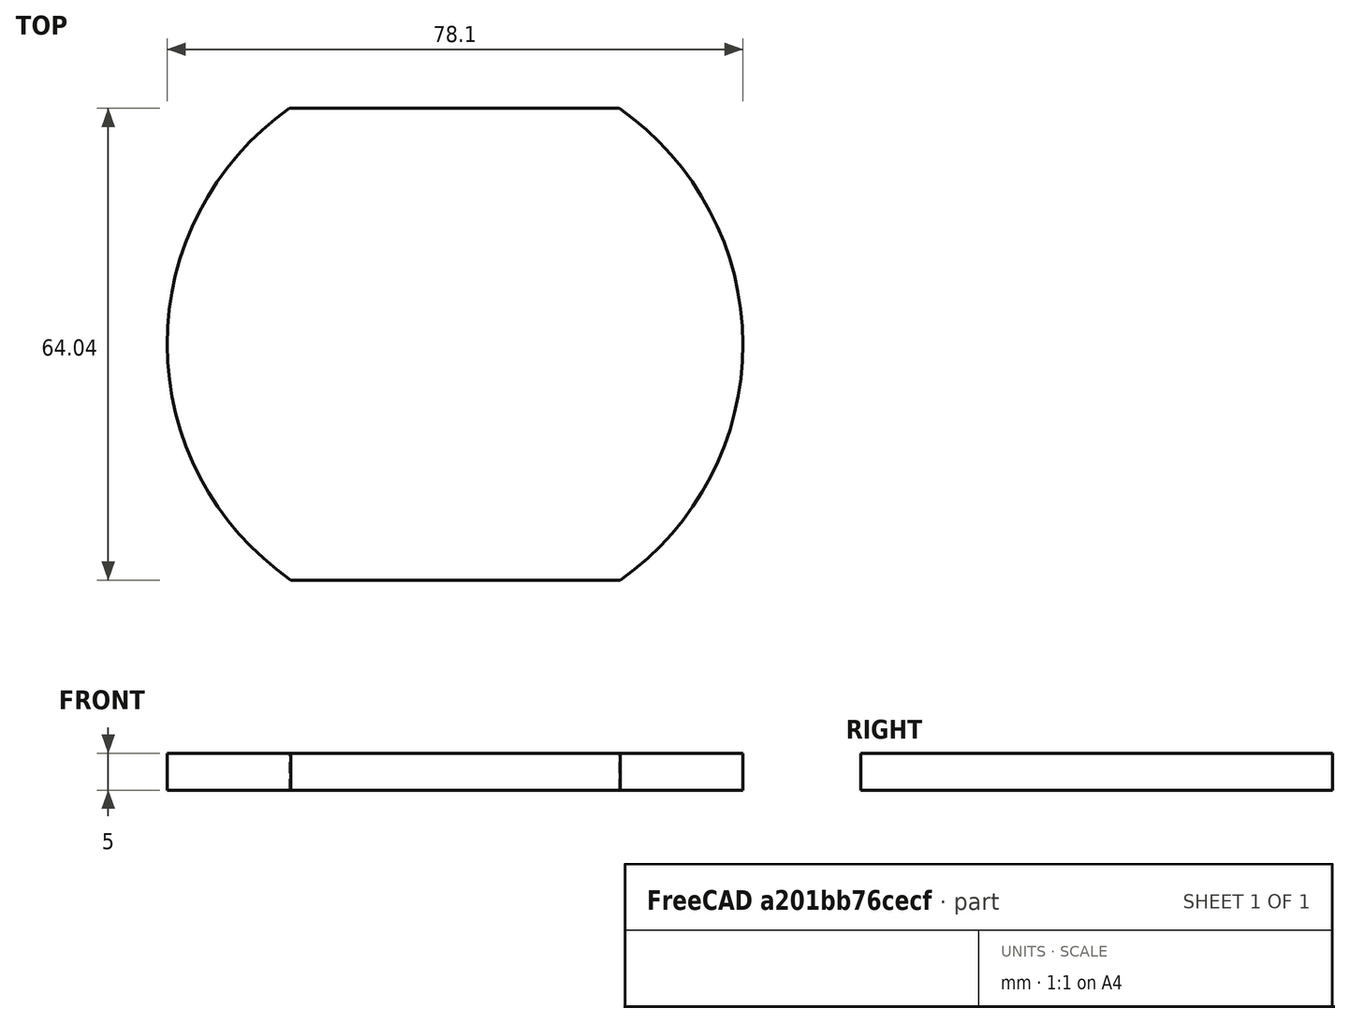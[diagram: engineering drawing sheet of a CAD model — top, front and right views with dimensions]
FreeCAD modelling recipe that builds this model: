
FCSTD DOCUMENT  (FreeCAD 1.0R39319 (Git))
Label: test_chord_volume
License: All rights reserved
LicenseURL: https://en.wikipedia.org/wiki/All_rights_reserved
objects: Sketcher::SketchObject×1, PartDesign::Pad×1, PartDesign::Body×1
note: 6 computed .brp shape members not serialized (recipe doc carries the construction recipe); baked Part::Feature solids carry a one-line shape summary decoded from their .brp

FEATURE [Sketcher::SketchObject] Sketch_1
  ArcFitTolerance = 1e-06
  AttachmentSupport = -> [XY_Plane]
  FullyConstrained = false
  MakeInternals = false
  MapMode = 5
  sketch-geometry (4):
    g0: ArcOfCircle CenterX=-0.00134482 CenterY=-7.04804 CenterZ=0 NormalX=0 NormalY=0 NormalZ=1 AngleXU=0 Radius=39.0492 StartAngle=5.32437 EndAngle=7.24728
    g1: LineSegment StartX=22.2629 StartY=25.0323 StartZ=0 EndX=-22.4507 EndY=25.0323 EndZ=0
    g2: ArcOfCircle CenterX=0.00211821 CenterY=-6.92347 CenterZ=0 NormalX=0 NormalY=0 NormalZ=1 AngleXU=0 Radius=39.0551 StartAngle=2.18328 EndAngle=4.10577
    g3: LineSegment StartX=-22.2629 StartY=-39.0104 StartZ=0 EndX=22.4319 EndY=-39.0104 EndZ=0
  constraints (7):
    c: Coincident(g0,g1)
    c: Coincident(g1,g2)
    c: Coincident(g2,g3)
    c: Coincident(g3,g0)
    c: Parallel(g1,g3)
    c: Horizontal(g1)
    c: Distance(g1,g3) = 78
FEATURE [PartDesign::Pad] Pad_1
  Direction = (0,0,1)
  Length = 5
  Length2 = 10
  Profile = -> Sketch_1
  Refine = true
  Suppressed = false
  Type = 0
FEATURE [PartDesign::Body] Body
  AllowCompound = false
  Group = -> [Sketch_1,Pad_1]
  Origin = -> Origin
  Tip = -> Pad_1
